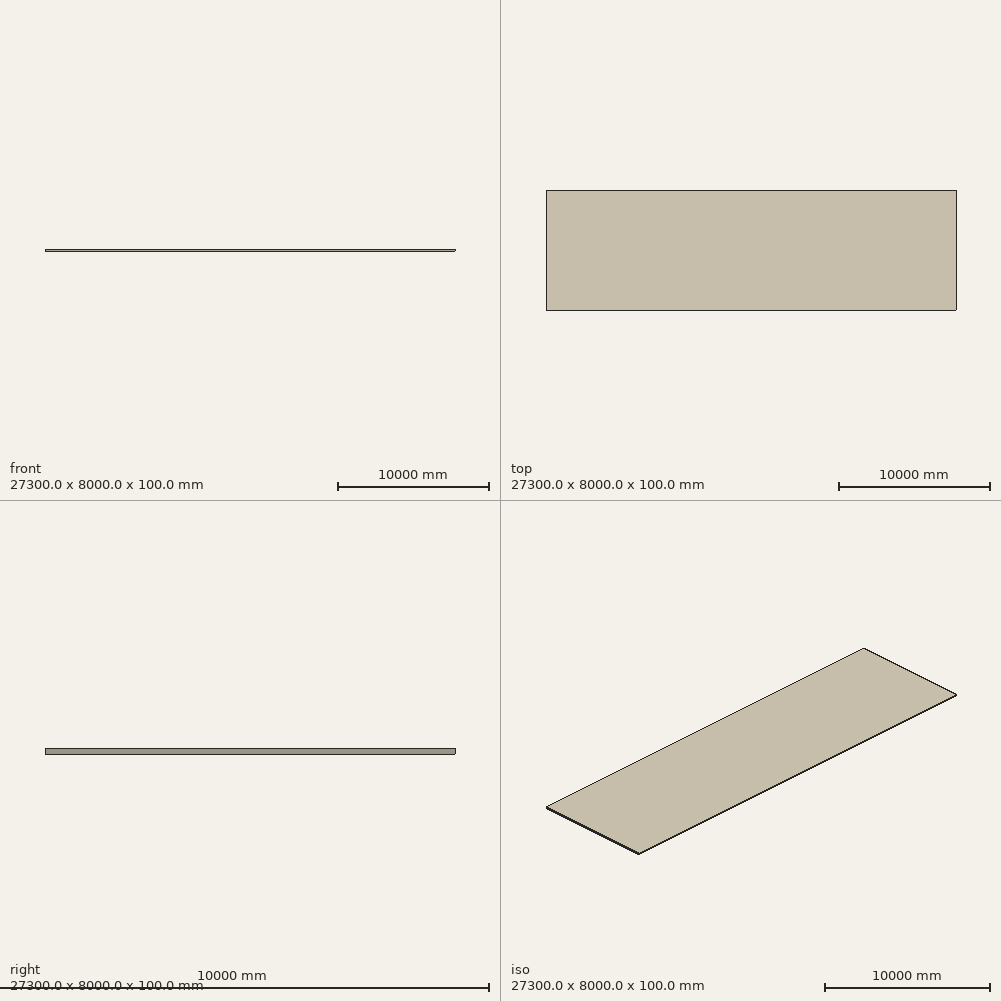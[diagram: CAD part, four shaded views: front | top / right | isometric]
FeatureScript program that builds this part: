
annotation { "Feature Type Name" : "Feature", "Feature Type Description" : "" }
export const myFeature = defineFeature(function(context is Context, id is Id, definition is map)
    precondition{}
    {
        {
            var Q0;
            Q0=qCreatedBy(makeId("Top.planeOp"),FACE);
            var sketch = newSketch(context, id + "F0", { "sketchPlane" : qUnion([Q0])});
            skLineSegment(sketch, "E0.bottom", {"start": v(-13604.53, 4213.46) * mm, "end": v(13695.47, 4213.46) * mm});
            skLineSegment(sketch, "E0.top", {"start": v(-13604.53, -3786.54) * mm, "end": v(13695.47, -3786.54) * mm});
            skLineSegment(sketch, "E0.left", {"start": v(-13604.53, 4213.46) * mm, "end": v(-13604.53, -3786.54) * mm});
            skLineSegment(sketch, "E0.right", {"start": v(13695.47, 4213.46) * mm, "end": v(13695.47, -3786.54) * mm});
            skSolve(sketch);
        }
        {
            var Q0;
            Q0 = qSketchRegion(id + "F0", true);
            extrude(context, id + "F1", {"entities" : qUnion([Q0]), "depth" : 100 * mm});
        }
    });
